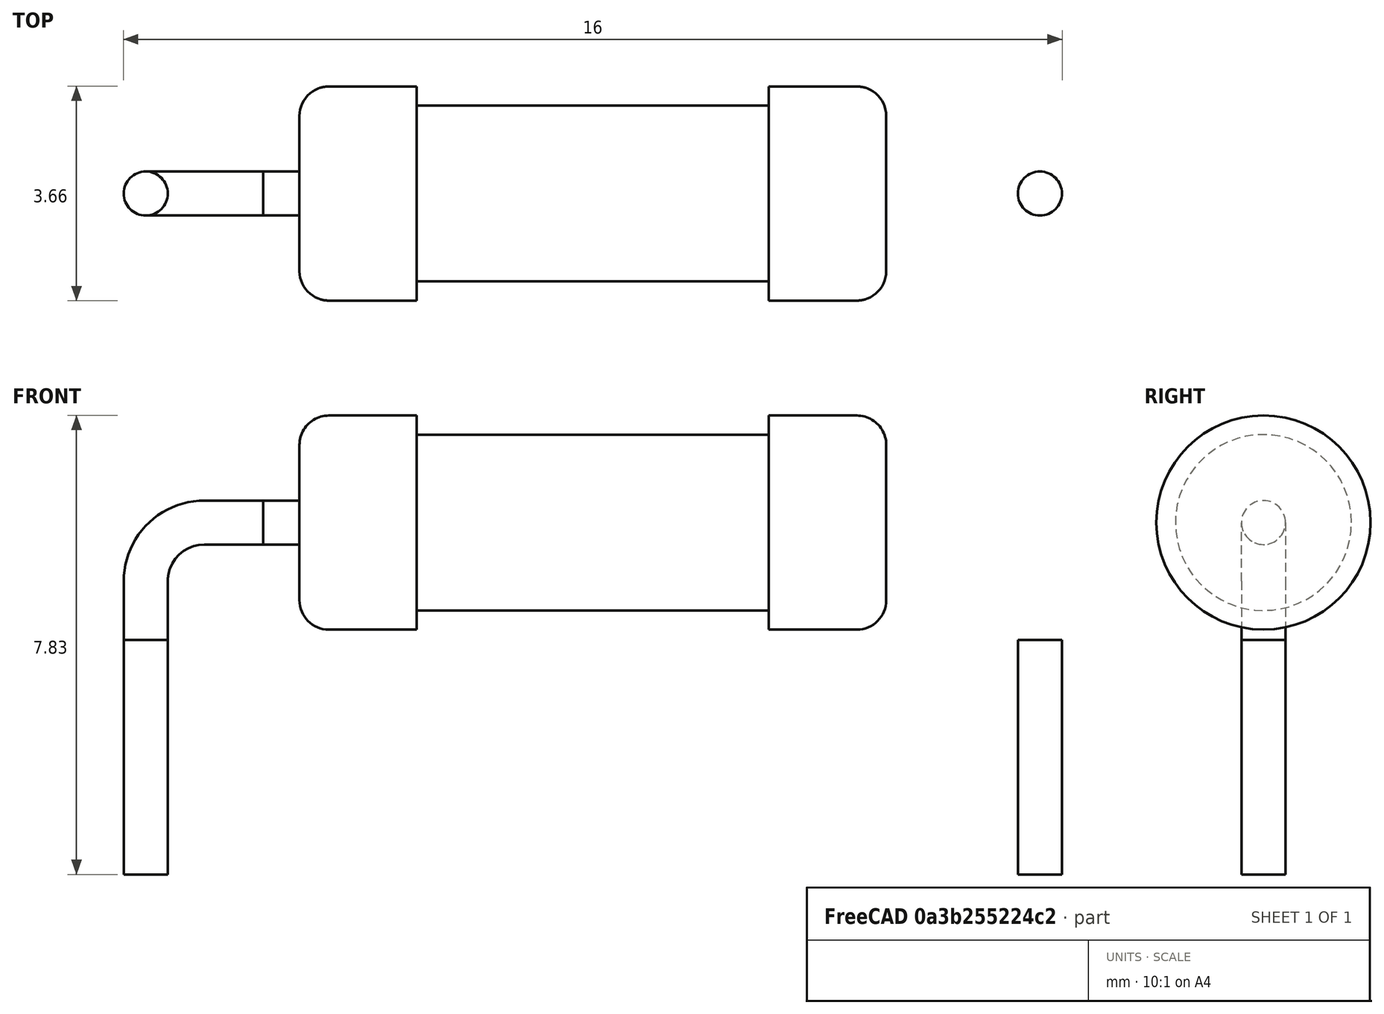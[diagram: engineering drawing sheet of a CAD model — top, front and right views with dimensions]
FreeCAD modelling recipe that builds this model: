
FCSTD DOCUMENT  (FreeCAD 0.18.4R)
Label: soviet_1w_dip
License: All rights reserved
LicenseURL: http://en.wikipedia.org/wiki/All_rights_reserved
objects: Part::Cylinder×6, Part::Mirroring×3, Part::Fillet×2, Part::Sweep×1
note: 12 computed .brp shape members not serialized (recipe doc carries the construction recipe); baked Part::Feature solids carry a one-line shape summary decoded from their .brp

FEATURE [Part::Cylinder] Cylinder
  Angle = 360
  AttacherType = Attacher::AttachEngine3D
  Height = 4
  Placement = pos=(-7.62,0,-2) rot=(0,0,1;0rad)
  Radius = 0.375
  expr: Radius = 0.75 / 2
FEATURE [Part::Cylinder] Cylinder001
  Angle = 360
  AttacherType = Attacher::AttachEngine3D
  Height = 4
  Placement = pos=(7.62,0,-2) rot=(0,0,1;0rad)
  Radius = 0.375
  expr: Radius = 0.75 / 2
FEATURE [Part::Cylinder] Cylinder002
  Angle = 360
  AttacherType = Attacher::AttachEngine3D
  Height = 2
  Placement = pos=(3,0,4) rot=(0,1,0;1.5708rad)
  Radius = 1.825
  expr: Radius = 3.65 / 2
FEATURE [Part::Cylinder] Cylinder003
  Angle = 360
  AttacherType = Attacher::AttachEngine3D
  Height = 6
  Placement = pos=(-3,0,4) rot=(0,1,0;1.5708rad)
  Radius = 1.5
FEATURE [Part::Cylinder] Cylinder004
  Angle = 360
  AttacherType = Attacher::AttachEngine3D
  Height = 2
  Placement = pos=(-5,0,4) rot=(0,1,0;1.5708rad)
  Radius = 1.825
  expr: Radius = 3.65 / 2
FEATURE [Part::Fillet] Fillet
  Base = -> Cylinder002
  Edges = 1 edges r=0.5: [Edge1]
FEATURE [Part::Fillet] Fillet001
  Base = -> Cylinder004
  Edges = 1 edges r=0.5: [Edge3]
FEATURE [Part::Sweep] Sweep
  Frenet = false
  Solid = true
  Transition = 1
FEATURE [Part::Mirroring] Part__Mirroring  label="Sweep (Mirror #1)"
  Base = (0,0,0)
  Normal = (0,0,1)
  Placement = pos=(5.62,0,4) rot=(0,0,1;0rad)
  Source = -> Sweep
FEATURE [Part::Mirroring] Part__Mirroring001  label="Sweep (Mirror #2)"
  Base = (0,0,0)
  Normal = (1,0,0)
  Source = -> Part__Mirroring
FEATURE [Part::Cylinder] Cylinder005
  Angle = 360
  AttacherType = Attacher::AttachEngine3D
  Height = 0.62
  Placement = pos=(5,0,4) rot=(0,1,0;1.5708rad)
  Radius = 0.375
FEATURE [Part::Mirroring] Part__Mirroring002  label="Cylinder005 (Mirror #3)"
  Base = (0,0,0)
  Normal = (1,0,0)
  Source = -> Cylinder005
